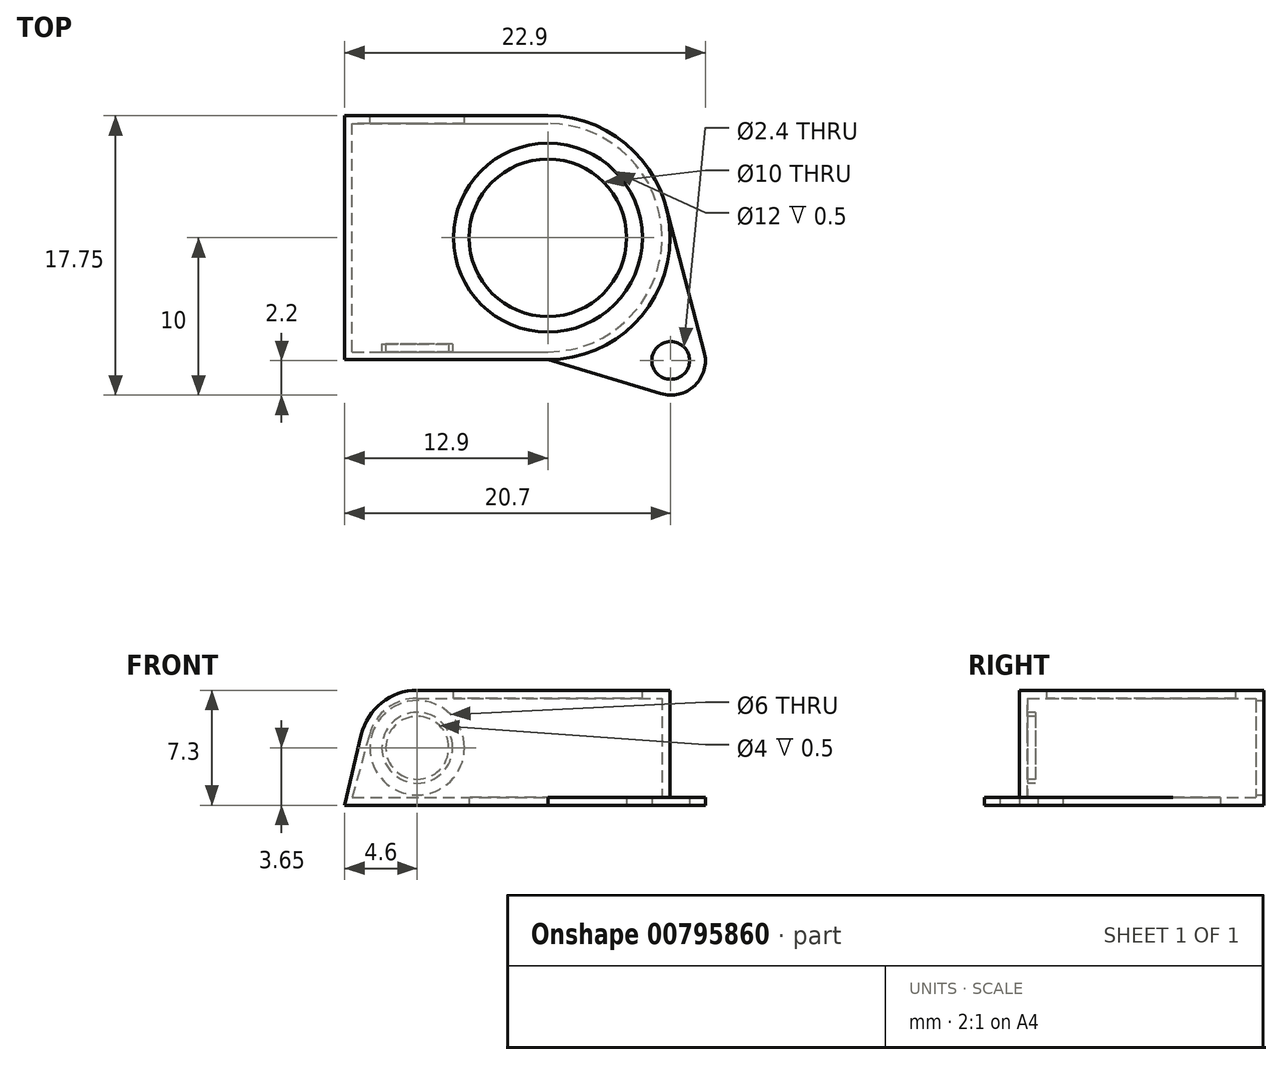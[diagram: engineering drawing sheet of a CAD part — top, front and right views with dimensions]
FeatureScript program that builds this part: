
annotation { "Feature Type Name" : "Feature", "Feature Type Description" : "" }
export const myFeature = defineFeature(function(context is Context, id is Id, definition is map)
    precondition{}
    {
        {
            var Q0;
            Q0=qCreatedBy(makeId("Top.planeOp"),FACE);
            var sketch = newSketch(context, id + "F0", { "sketchPlane" : qUnion([Q0])});
            skLineSegment(sketch, "E0.bottom", {"start": v(-12.9, 7.75) * mm, "end": v(10, 7.75) * mm, "construction": true});
            skLineSegment(sketch, "E0.top", {"start": v(-12.9, -10) * mm, "end": v(10, -10) * mm, "construction": true});
            skLineSegment(sketch, "E0.left", {"start": v(-12.9, 7.75) * mm, "end": v(-12.9, -10) * mm, "construction": true});
            skLineSegment(sketch, "E0.right", {"start": v(10, 7.75) * mm, "end": v(10, -10) * mm, "construction": true});
            skLineSegment(sketch, "E1", {"start": v(7.8, -7.8) * mm, "end": v(7.8, -10) * mm, "construction": true});
            skLineSegment(sketch, "E2", {"start": v(7.8, -10) * mm, "end": v(10, -10) * mm, "construction": true});
            skCircle(sketch, "E3", {"center": v(7.8, -7.8) * mm, "radius": 1.2 * mm});
            skLineSegment(sketch, "E4", {"start": v(-12.9, 7.75) * mm, "end": v(-12.9, -7.75) * mm});
            skArc(sketch, "E5", {"start": v(0, 7.75) * mm, "mid": v(7.75, 0) * mm, "end": v(0, -7.75) * mm});
            skLineSegment(sketch, "E6", {"start": v(0, 7.75) * mm, "end": v(-12.9, 7.75) * mm});
            skLineSegment(sketch, "E7", {"start": v(0, -7.75) * mm, "end": v(-12.9, -7.75) * mm});
            skArc(sketch, "E8", {"start": v(7.17, -9.9) * mm, "mid": v(9.33, -9.38) * mm, "end": v(9.93, -7.24) * mm});
            skLineSegment(sketch, "E9", {"start": v(0, -7.75) * mm, "end": v(7.17, -9.9) * mm});
            skLineSegment(sketch, "E10", {"start": v(9.93, -7.24) * mm, "end": v(7.5, 1.98) * mm});
            skCircle(sketch, "E11", {"center": v(0, 0) * mm, "radius": 5 * mm});
            skLineSegment(sketch, "E12", {"start": v(0, 7.75) * mm, "end": v(0, -7.75) * mm, "construction": true});
            skLineSegment(sketch, "E13", {"start": v(-8.3, 7.75) * mm, "end": v(-8.3, -7.75) * mm, "construction": true});
            skLineSegment(sketch, "E14", {"start": v(-5.9, 7.75) * mm, "end": v(-5.9, -7.75) * mm, "construction": true});
            skLineSegment(sketch, "E15", {"start": v(-6.3, 7.75) * mm, "end": v(-6.3, -7.75) * mm, "construction": true});
            skLineSegment(sketch, "E16", {"start": v(-10.3, 7.75) * mm, "end": v(-10.3, -7.75) * mm, "construction": true});
            skCircle(sketch, "E17", {"center": v(0, 0) * mm, "radius": 5 * mm, "construction": true});
            skCircle(sketch, "E18", {"center": v(0, 0) * mm, "radius": 5.9 * mm, "construction": true});
            skLineSegment(sketch, "E19", {"start": v(-11.2, 7.75) * mm, "end": v(-11.2, -7.75) * mm, "construction": true});
            skLineSegment(sketch, "E20", {"start": v(-5.4, 7.75) * mm, "end": v(-5.4, -7.75) * mm, "construction": true});
            skSolve(sketch);
        }
        {
            var Q0;
            Q0 = qSketchRegion(id + "F0", true);
            extrude(context, id + "F1", {"entities" : qUnion([Q0]), "depth" : 0.5 * mm, "offsetDistance" : 25 * mm});
        }
        {
            var Q0;
            Q0=qCreatedBy(makeId("Top.planeOp"),FACE);
            var sketch = newSketch(context, id + "F2", { "sketchPlane" : qUnion([Q0])});
            skLineSegment(sketch, "E21", {"start": v(-12.93, -7.75) * mm, "end": v(0, -7.75) * mm});
            skLineSegment(sketch, "E22", {"start": v(-12.93, -7.75) * mm, "end": v(-12.93, 7.75) * mm});
            skLineSegment(sketch, "E23", {"start": v(-12.93, 7.75) * mm, "end": v(0, 7.75) * mm});
            skArc(sketch, "E24", {"start": v(0, 7.75) * mm, "mid": v(7.75, 0) * mm, "end": v(0, -7.75) * mm});
            skLineSegment(sketch, "E25", {"start": v(-12.4, 7.25) * mm, "end": v(-12.4, -7.25) * mm});
            skLineSegment(sketch, "E26", {"start": v(-12.4, -7.25) * mm, "end": v(0, -7.25) * mm});
            skLineSegment(sketch, "E27", {"start": v(-12.4, 7.25) * mm, "end": v(0, 7.25) * mm});
            skArc(sketch, "E28", {"start": v(0, 7.25) * mm, "mid": v(7.25, 0) * mm, "end": v(0, -7.25) * mm});
            skSolve(sketch);
        }
        {
            var Q0;
            Q0 = qSketchRegion(id + "F2", true);
            extrude(context, id + "F3", {"entities" : qUnion([Q0]), "operationType" : NewBodyOperationType.ADD, "depth" : 7.3 * mm, "offsetDistance" : 25 * mm, "hasSecondDirection" : true, "secondDirectionOppositeDirection" : false, "secondDirectionDepth" : 0.5 * mm});
        }
        {
            var Q0;
            Q0=makeQuery(id+"F3.boolean.opBoolean","MERGE",FACE,{"derivedFrom":[makeQuery(id+"F1.opExtrude","SWEPT_FACE",FACE,{"disambiguationData":[OSD([sQuery(id+"F0.wireOp",EDGE,"E6")])]}),makeQuery(id+"F3.opExtrude","SWEPT_FACE",FACE,{"disambiguationData":[OSD([sQuery(id+"F2.wireOp",EDGE,"E23")])]})]});
            var sketch = newSketch(context, id + "F4", { "sketchPlane" : qUnion([Q0])});
            skLineSegment(sketch, "E29", {"start": v(8.3, 0) * mm, "end": v(8.3, 7.3) * mm, "construction": true});
            skCircle(sketch, "E30", {"center": v(8.3, 3.65) * mm, "radius": 3 * mm});
            skSolve(sketch);
        }
        {
            var Q0;
            Q0 = qSketchRegion(id + "F4", true);
            extrude(context, id + "F5", {"entities" : qUnion([Q0]), "operationType" : NewBodyOperationType.REMOVE, "endBound" : BoundingType.UP_TO_NEXT, "oppositeDirection" : true, "depth" : 25 * mm, "offsetDistance" : 25 * mm});
        }
        {
            var Q0;
            Q0=makeQuery(id+"F3.opExtrude","SWEPT_FACE",FACE,{"disambiguationData":[OSD([sQuery(id+"F2.wireOp",EDGE,"E26")])]});
            var sketch = newSketch(context, id + "F6", { "sketchPlane" : qUnion([Q0])});
            skCircle(sketch, "E31", {"center": v(8.3, 3.65) * mm, "radius": 2 * mm});
            skLineSegment(sketch, "E32", {"start": v(8.3, 0) * mm, "end": v(8.3, 7.3) * mm, "construction": true});
            skCircle(sketch, "E33", {"center": v(8.3, 3.65) * mm, "radius": 2.25 * mm});
            skSolve(sketch);
        }
        {
            var Q0;
            Q0 = qSketchRegion(id + "F6", true);
            extrude(context, id + "F7", {"entities" : qUnion([Q0]), "operationType" : NewBodyOperationType.ADD, "depth" : 0.5 * mm, "offsetDistance" : 25 * mm});
        }
        {
            var Q0;
            Q0=makeQuery(id+"F3.boolean.opBoolean","MERGE",FACE,{"derivedFrom":[makeQuery(id+"F1.opExtrude","SWEPT_FACE",FACE,{"disambiguationData":[OSD([sQuery(id+"F0.wireOp",EDGE,"E6")])]}),makeQuery(id+"F3.opExtrude","SWEPT_FACE",FACE,{"disambiguationData":[OSD([sQuery(id+"F2.wireOp",EDGE,"E23")])]})]});
            var sketch = newSketch(context, id + "F8", { "sketchPlane" : qUnion([Q0])});
            skLineSegment(sketch, "E34", {"start": v(8.3, 0) * mm, "end": v(8.3, 7.3) * mm, "construction": true});
            skArc(sketch, "E35", {"start": v(8.3, 7.3) * mm, "mid": v(10.57, 6.5) * mm, "end": v(11.85, 4.48) * mm});
            skLineSegment(sketch, "E36", {"start": v(12.9, 0) * mm, "end": v(11.85, 4.48) * mm});
            skLineSegment(sketch, "E37", {"start": v(8.3, 7.3) * mm, "end": v(15.27, 7.3) * mm});
            skLineSegment(sketch, "E38", {"start": v(15.27, 7.3) * mm, "end": v(12.9, 0) * mm});
            skSolve(sketch);
        }
        {
            var Q0;
            Q0 = qSketchRegion(id + "F8", true);
            extrude(context, id + "F9", {"entities" : qUnion([Q0]), "operationType" : NewBodyOperationType.REMOVE, "endBound" : BoundingType.THROUGH_ALL, "oppositeDirection" : true, "depth" : 25 * mm, "offsetDistance" : 25 * mm});
        }
        {
            var Q0;
            {var subQ0=sQuery(id+"F0.wireOp",EDGE,"E11");Q0=makeQuery(id+"F3.boolean.opBoolean","SPLIT",FACE,{"disambiguationData":[TD([makeQuery(id+"F1.opExtrude","SWEPT_FACE",FACE,{"disambiguationData":[OSD([subQ0])]})])],"derivedFrom":makeQuery(id+"F1.opExtrude","CAP_FACE",FACE,{"disambiguationData":[OSD([sQuery(id+"F0.wireOp",EDGE,"E3"),sQuery(id+"F0.wireOp",EDGE,"E4"),sQuery(id+"F0.wireOp",EDGE,"E5"),sQuery(id+"F0.wireOp",EDGE,"E6"),sQuery(id+"F0.wireOp",EDGE,"E7"),sQuery(id+"F0.wireOp",EDGE,"E8"),sQuery(id+"F0.wireOp",EDGE,"E9"),sQuery(id+"F0.wireOp",EDGE,"E10"),subQ0])],"isStart":false})});}
            var sketch = newSketch(context, id + "F10", { "sketchPlane" : qUnion([Q0])});
            skLineSegment(sketch, "E39.bottom", {"start": v(-11.2, 7.25) * mm, "end": v(-12.9, 7.25) * mm});
            skLineSegment(sketch, "E39.top", {"start": v(-11.2, -7.25) * mm, "end": v(-12.9, -7.25) * mm});
            skLineSegment(sketch, "E39.left", {"start": v(-11.2, 7.25) * mm, "end": v(-11.2, -7.25) * mm});
            skLineSegment(sketch, "E39.right", {"start": v(-12.9, 7.25) * mm, "end": v(-12.9, -7.25) * mm});
            skSolve(sketch);
        }
        {
            var Q0;
            Q0 = qSketchRegion(id + "F10", true);
            extrude(context, id + "F11", {"entities" : qUnion([Q0]), "operationType" : NewBodyOperationType.REMOVE, "depth" : 25 * mm, "offsetDistance" : 25 * mm});
        }
        {
            var Q0;
            Q0=makeQuery(id+"F11.boolean.opBoolean","MERGE",FACE,{"derivedFrom":[makeQuery(id+"F3.opExtrude","SWEPT_FACE",FACE,{"disambiguationData":[OSD([sQuery(id+"F2.wireOp",EDGE,"E27")])]}),makeQuery(id+"F11.opExtrude","SWEPT_FACE",FACE,{"disambiguationData":[OSD([sQuery(id+"F10.wireOp",EDGE,"E39.bottom")])]})]});
            var sketch = newSketch(context, id + "F12", { "sketchPlane" : qUnion([Q0])});
            skLineSegment(sketch, "E40", {"start": v(-8.3, 0) * mm, "end": v(-8.3, 7.3) * mm, "construction": true});
            skLineSegment(sketch, "E41", {"start": v(-8.3, 7.3) * mm, "end": v(-8.3, 6.8) * mm});
            skArc(sketch, "E42", {"start": v(-8.3, 7.3) * mm, "mid": v(-10.57, 6.5) * mm, "end": v(-11.85, 4.48) * mm});
            skArc(sketch, "E43", {"start": v(-8.3, 6.8) * mm, "mid": v(-10.21, 6.15) * mm, "end": v(-11.34, 4.48) * mm});
            skLineSegment(sketch, "E44", {"start": v(-11.85, 4.48) * mm, "end": v(-12.78, 0.5) * mm});
            skLineSegment(sketch, "E45", {"start": v(-11.34, 4.48) * mm, "end": v(-12.43, 0.5) * mm});
            skLineSegment(sketch, "E46", {"start": v(-12.78, 0.5) * mm, "end": v(-12.43, 0.5) * mm});
            skSolve(sketch);
        }
        {
            var Q0;
            Q0 = qSketchRegion(id + "F12", true);
            extrude(context, id + "F13", {"entities" : qUnion([Q0]), "operationType" : NewBodyOperationType.ADD, "endBound" : BoundingType.UP_TO_NEXT, "depth" : 25 * mm, "offsetDistance" : 25 * mm});
        }
        {
            var Q0;
            Q0=makeQuery(id+"F3.opExtrude","CAP_FACE",FACE,{"disambiguationData":[OSD([sQuery(id+"F2.wireOp",EDGE,"E21"),sQuery(id+"F2.wireOp",EDGE,"E22"),sQuery(id+"F2.wireOp",EDGE,"E23"),sQuery(id+"F2.wireOp",EDGE,"E24"),sQuery(id+"F2.wireOp",EDGE,"E25"),sQuery(id+"F2.wireOp",EDGE,"E26"),sQuery(id+"F2.wireOp",EDGE,"E27"),sQuery(id+"F2.wireOp",EDGE,"E28")])],"isStart":false});
            var sketch = newSketch(context, id + "F14", { "sketchPlane" : qUnion([Q0])});
            skLineSegment(sketch, "E47", {"start": v(-8.3, 7.25) * mm, "end": v(-8.3, -7.25) * mm});
            skLineSegment(sketch, "E48", {"start": v(-8.3, -7.25) * mm, "end": v(0, -7.25) * mm});
            skLineSegment(sketch, "E49", {"start": v(0, -7.25) * mm, "end": v(0, 7.25) * mm, "construction": true});
            skLineSegment(sketch, "E50", {"start": v(0, 7.25) * mm, "end": v(-8.3, 7.25) * mm});
            skArc(sketch, "E51", {"start": v(0, 7.25) * mm, "mid": v(7.25, 0) * mm, "end": v(0, -7.25) * mm});
            skCircle(sketch, "E52", {"center": v(0, 0) * mm, "radius": 6 * mm});
            skSolve(sketch);
        }
        {
            var Q0;
            Q0 = qSketchRegion(id + "F14", true);
            extrude(context, id + "F15", {"entities" : qUnion([Q0]), "operationType" : NewBodyOperationType.ADD, "oppositeDirection" : true, "depth" : 0.5 * mm, "offsetDistance" : 25 * mm});
        }
    });
